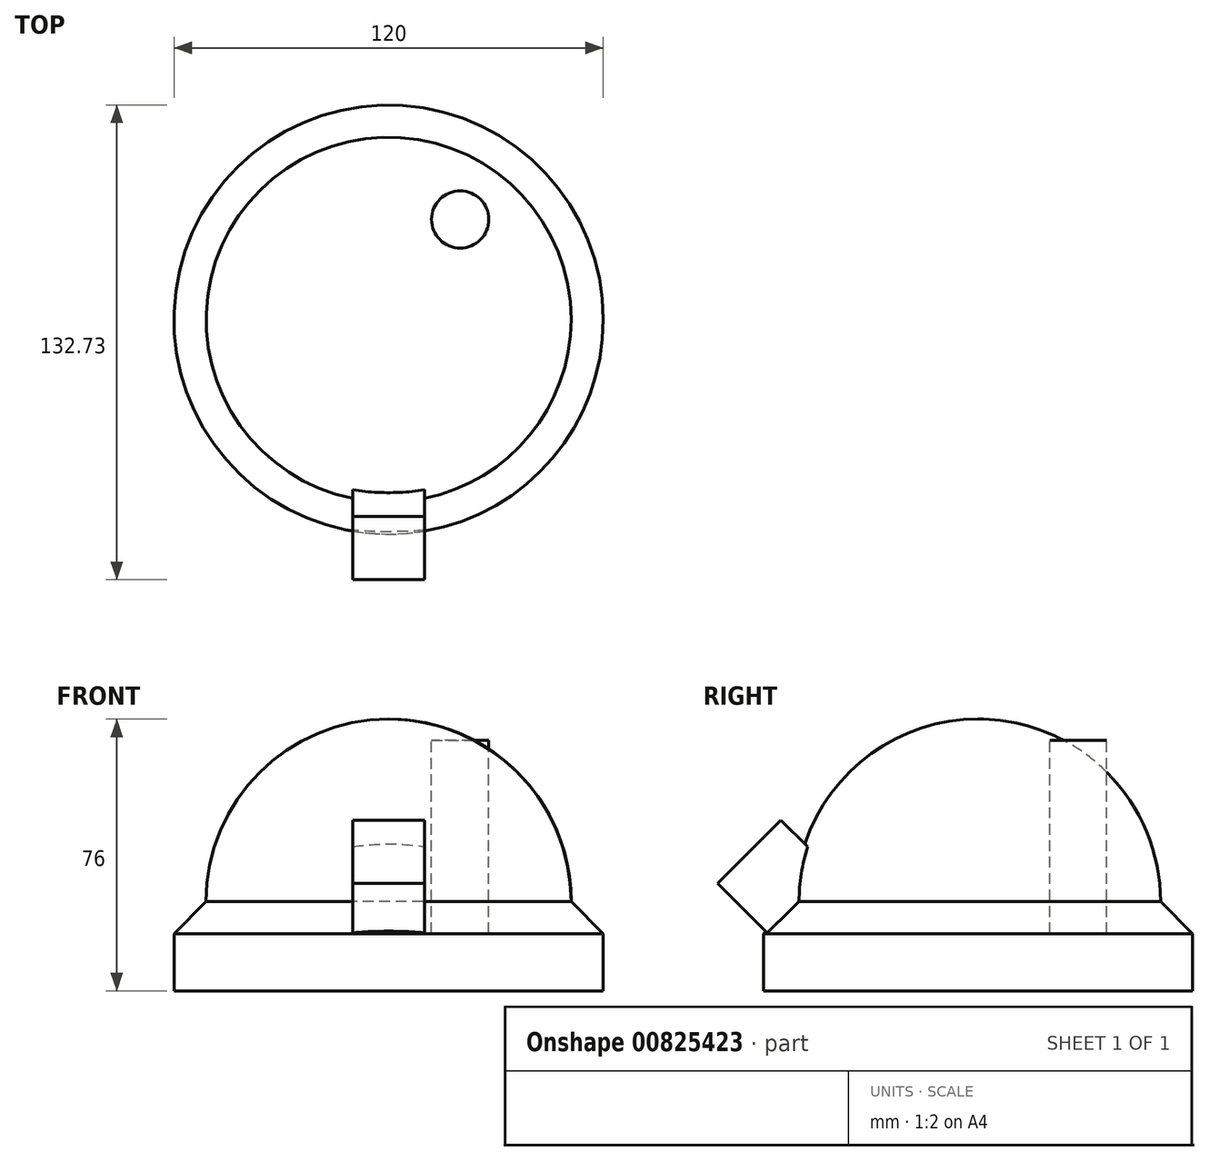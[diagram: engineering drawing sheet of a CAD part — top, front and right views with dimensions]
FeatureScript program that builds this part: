
annotation { "Feature Type Name" : "Feature", "Feature Type Description" : "" }
export const myFeature = defineFeature(function(context is Context, id is Id, definition is map)
    precondition{}
    {
        {
            var Q0;
            Q0=qCreatedBy(makeId("Top.planeOp"),FACE);
            var sketch = newSketch(context, id + "F0", { "sketchPlane" : qUnion([Q0])});
            skCircle(sketch, "E0", {"center": v(0, 0) * mm, "radius": 60 * mm});
            skSolve(sketch);
        }
        {
            var Q0;
            Q0=makeQuery(id+"F0.imprint","IMPRINT",FACE,{"disambiguationData":[TD([[makeQuery(id+"F0.imprint","IMPRINT",EDGE,{"derivedFrom":sQuery(id+"F0.wireOp",EDGE,"E0")}),1.0]])]});
            extrude(context, id + "F1", {"entities" : qUnion([Q0]), "depth" : 25 * mm, "offsetDistance" : 25 * mm});
        }
        {
            var Q0;
            Q0=makeQuery(id+"F1.opExtrude","CAP_EDGE",EDGE,{"disambiguationData":[OSD([sQuery(id+"F0.wireOp",EDGE,"E0")])],"isStart":false});
            chamfer(context, id + "F2", {"entities" : qUnion([Q0]), "width" : 9 * mm, "tangentPropagation" : true});
        }
        {
            var Q0;
            Q0=qCreatedBy(makeId("Front.planeOp"),FACE);
            var sketch = newSketch(context, id + "F3", { "sketchPlane" : qUnion([Q0])});
            skArc(sketch, "E1", {"start": v(51, 25) * mm, "mid": v(36.06, 61.06) * mm, "end": v(0, 76) * mm});
            skLineSegment(sketch, "E2", {"start": v(0, 25) * mm, "end": v(0, 76) * mm});
            skLineSegment(sketch, "E3", {"start": v(0, 25) * mm, "end": v(51, 25) * mm});
            skSolve(sketch);
        }
        {
            var Q0;
            Q0=makeQuery(id+"F3.imprint","IMPRINT",FACE,{"disambiguationData":[TD([[makeQuery(id+"F3.imprint","IMPRINT",EDGE,{"derivedFrom":sQuery(id+"F3.wireOp",EDGE,"E1")}),1.0]])]});
            var Q1;
            Q1=sQuery(id+"F3.wireOp",EDGE,"E2");
            revolve(context, id + "F4", {"operationType" : NewBodyOperationType.ADD, "surfaceOperationType" : NewSurfaceOperationType.NEW, "entities" : qUnion([Q0]), "axis" : qUnion([Q1]), "revolveType" : RevolveType.FULL});
        }
        {
            var Q0;
            Q0=qCreatedBy(makeId("Top.planeOp"),FACE);
            cPlane(context, id + "F5", {"entities" : qUnion([Q0]), "cplaneType" : CPlaneType.OFFSET, "offset" : 70 * mm, "width" : 150 * mm, "height" : 150 * mm});
        }
        {
            var Q0;
            Q0=qCreatedBy(id+"F5.planeOp",FACE);
            var sketch = newSketch(context, id + "F6", { "sketchPlane" : qUnion([Q0])});
            skCircle(sketch, "E4", {"center": v(20, 28) * mm, "radius": 8 * mm});
            skLineSegment(sketch, "E5", {"start": v(20, 28) * mm, "end": v(0, 28) * mm, "construction": true});
            skLineSegment(sketch, "E6", {"start": v(20, 28) * mm, "end": v(20, 0) * mm, "construction": true});
            skCircle(sketch, "E7.MirrorC", {"center": v(-20, 28) * mm, "radius": 8 * mm});
            skSolve(sketch);
        }
        {
            var Q0;
            Q0=makeQuery(id+"F6.imprint","IMPRINT",FACE,{"disambiguationData":[TD([[makeQuery(id+"F6.imprint","IMPRINT",EDGE,{"derivedFrom":sQuery(id+"F6.wireOp",EDGE,"E7.MirrorC")}),-1.0]])]});
            var Q1;
            Q1=makeQuery(id+"F6.imprint","IMPRINT",FACE,{"disambiguationData":[TD([[makeQuery(id+"F6.imprint","IMPRINT",EDGE,{"derivedFrom":sQuery(id+"F6.wireOp",EDGE,"E4")}),1.0]])]});
            extrude(context, id + "F7", {"entities" : qUnion([Q0, Q1]), "oppositeDirection" : true, "depth" : 53.9 * mm, "offsetDistance" : 25 * mm});
        }
        {
            var Q0;
            Q0=qCreatedBy(makeId("Top.planeOp"),FACE);
            cPlane(context, id + "F8", {"entities" : qUnion([Q0]), "cplaneType" : CPlaneType.OFFSET, "offset" : 25 * mm, "width" : 150 * mm, "height" : 150 * mm});
        }
        {
            var Q0;
            Q0=qCreatedBy(id+"F8.planeOp",FACE);
            var sketch = newSketch(context, id + "F9", { "sketchPlane" : qUnion([Q0])});
            skLineSegment(sketch, "E8", {"start": v(-75.03, 0) * mm, "end": v(74.85, 0) * mm, "construction": true});
            skSolve(sketch);
        }
        {
            var Q0;
            Q0=qCreatedBy(id+"F8.planeOp",FACE);
            var Q1;
            Q1=sQuery(id+"F9.wireOp",EDGE,"E8");
            cPlane(context, id + "F10", {"entities" : qUnion([Q0, Q1]), "cplaneType" : CPlaneType.LINE_ANGLE, "offset" : 25 * mm, "angle" : 45 * degree, "width" : 150 * mm, "height" : 150 * mm});
        }
        {
            var Q0;
            Q0=qCreatedBy(id+"F10.planeOp",FACE);
            cPlane(context, id + "F11", {"entities" : qUnion([Q0]), "cplaneType" : CPlaneType.OFFSET, "offset" : 55 * mm, "oppositeDirection" : true, "width" : 150 * mm, "height" : 150 * mm});
        }
        {
            var Q0;
            Q0=qCreatedBy(id+"F11.planeOp",FACE);
            var sketch = newSketch(context, id + "F12", { "sketchPlane" : qUnion([Q0])});
            skLineSegment(sketch, "E9.bottom", {"start": v(-10, -5.18) * mm, "end": v(10, -5.18) * mm});
            skLineSegment(sketch, "E9.top", {"start": v(-10, -30.18) * mm, "end": v(10, -30.18) * mm});
            skLineSegment(sketch, "E9.left", {"start": v(-10, -5.18) * mm, "end": v(-10, -30.18) * mm});
            skLineSegment(sketch, "E9.right", {"start": v(10, -5.18) * mm, "end": v(10, -30.18) * mm});
            skPoint(sketch, "E9.middle", {"position": v(0, -17.68) * mm});
            skSolve(sketch);
        }
        {
            var Q0;
            Q0=makeQuery(id+"F12.imprint","IMPRINT",FACE,{"disambiguationData":[TD([[makeQuery(id+"F12.imprint","IMPRINT",EDGE,{"derivedFrom":sQuery(id+"F12.wireOp",EDGE,"E9.bottom")}),-1.0]])]});
            extrude(context, id + "F13", {"entities" : qUnion([Q0]), "operationType" : NewBodyOperationType.ADD, "depth" : 35 * mm, "offsetDistance" : 25 * mm});
        }
    });
